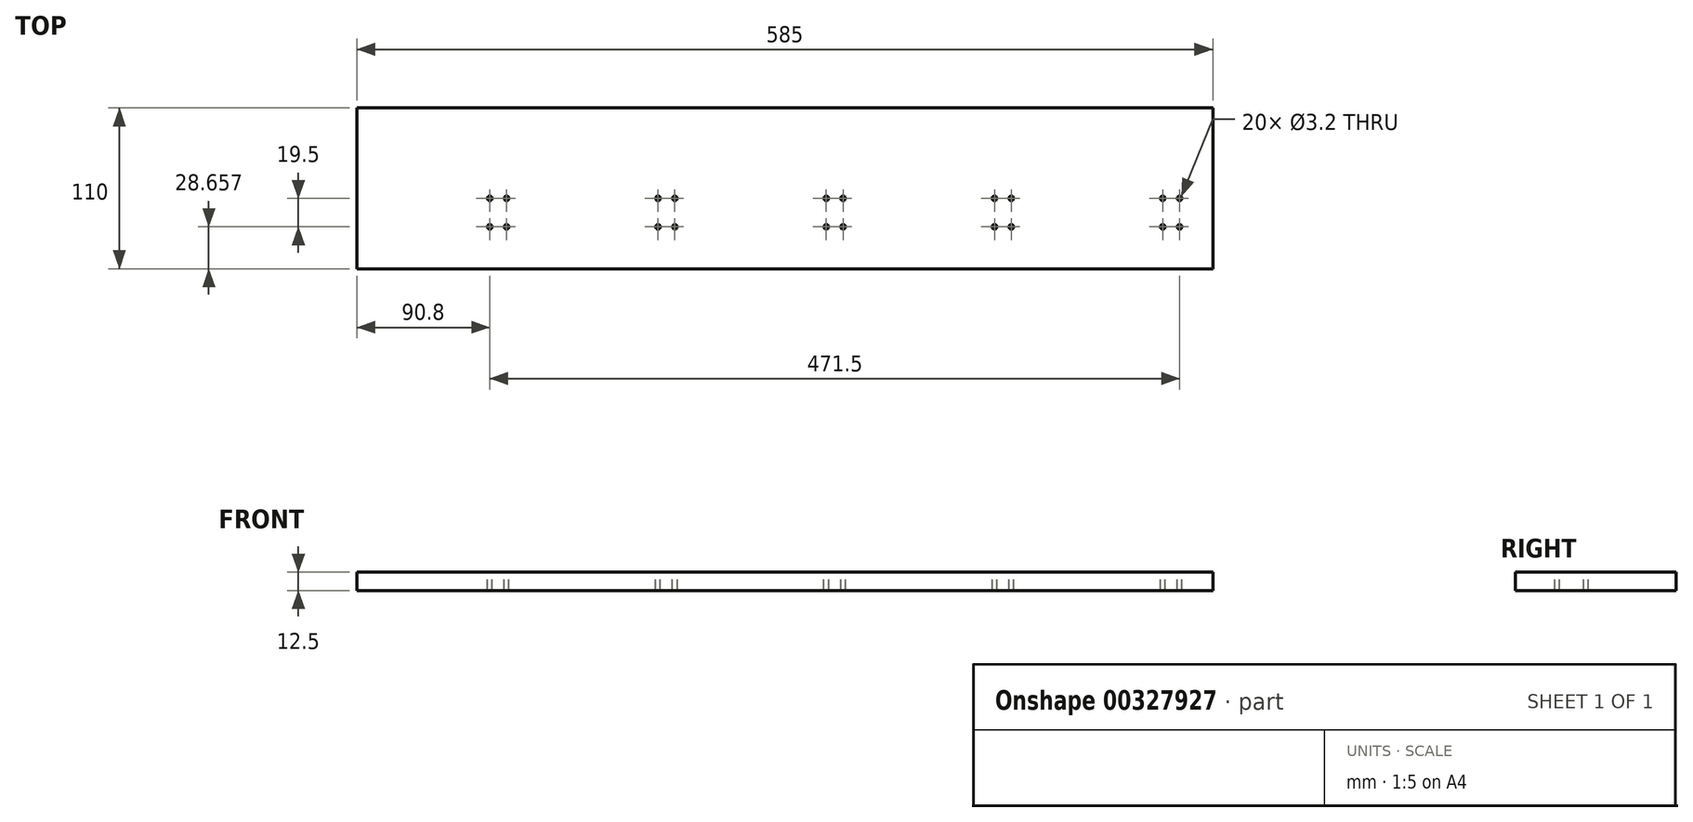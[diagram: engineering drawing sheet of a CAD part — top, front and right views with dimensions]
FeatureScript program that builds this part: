
annotation { "Feature Type Name" : "Feature", "Feature Type Description" : "" }
export const myFeature = defineFeature(function(context is Context, id is Id, definition is map)
    precondition{}
    {
        {
            var Q0;
            Q0=qCreatedBy(makeId("Top.planeOp"),FACE);
            var sketch = newSketch(context, id + "F0", { "sketchPlane" : qUnion([Q0])});
            skLineSegment(sketch, "E0.bottom", {"start": v(0, 0) * mm, "end": v(585, 0) * mm});
            skLineSegment(sketch, "E0.top", {"start": v(0, -110) * mm, "end": v(585, -110) * mm});
            skLineSegment(sketch, "E0.left", {"start": v(0, 0) * mm, "end": v(0, -110) * mm});
            skLineSegment(sketch, "E0.right", {"start": v(585, 0) * mm, "end": v(585, -110) * mm});
            skSolve(sketch);
        }
        {
            var Q0;
            Q0 = qSketchRegion(id + "F0", true);
            extrude(context, id + "F1", {"entities" : qUnion([Q0]), "depth" : 12.5 * mm});
        }
        {
            var Q0;
            Q0=makeQuery(id+"F1.opExtrude","CAP_FACE",FACE,{"disambiguationData":[OSD([sQuery(id+"F0.wireOp",EDGE,"E0.bottom"),sQuery(id+"F0.wireOp",EDGE,"E0.top"),sQuery(id+"F0.wireOp",EDGE,"E0.left"),sQuery(id+"F0.wireOp",EDGE,"E0.right")])],"isStart":false});
            var sketch = newSketch(context, id + "F2", { "sketchPlane" : qUnion([Q0])});
            skLineSegment(sketch, "E1.bottom", {"start": v(64.2, -65.1) * mm, "end": v(70.9, -65.1) * mm});
            skLineSegment(sketch, "E1.top", {"start": v(64.2, -78.1) * mm, "end": v(70.9, -78.1) * mm});
            skLineSegment(sketch, "E1.left", {"start": v(64.2, -65.1) * mm, "end": v(64.2, -78.1) * mm});
            skLineSegment(sketch, "E1.right", {"start": v(70.9, -65.1) * mm, "end": v(70.9, -78.1) * mm});
            skLineSegment(sketch, "E2.top", {"start": v(10, -95.2) * mm, "end": v(72.5, -95.2) * mm});
            skLineSegment(sketch, "E2.left", {"start": v(10, -10) * mm, "end": v(10, -95.2) * mm});
            skLineSegment(sketch, "E2.right", {"start": v(72.5, -10) * mm, "end": v(72.5, -95.2) * mm});
            skCircle(sketch, "E3", {"center": v(90.8, -61.84) * mm, "radius": 2 * mm});
            skCircle(sketch, "E4", {"center": v(90.8, -81.34) * mm, "radius": 2 * mm});
            skCircle(sketch, "E5", {"center": v(102.3, -61.84) * mm, "radius": 2 * mm});
            skCircle(sketch, "E6", {"center": v(102.3, -81.34) * mm, "radius": 2 * mm});
            skLineSegment(sketch, "E7", {"start": v(61.15, -71.6) * mm, "end": v(124.25, -71.6) * mm, "construction": true});
            skLineSegment(sketch, "E8.1.0.0", {"start": v(125, -95.2) * mm, "end": v(187.5, -95.2) * mm});
            skLineSegment(sketch, "E8.1.0.1", {"start": v(187.5, -10) * mm, "end": v(187.5, -95.2) * mm});
            skLineSegment(sketch, "E8.1.0.2", {"start": v(179.2, -65.1) * mm, "end": v(185.9, -65.1) * mm});
            skLineSegment(sketch, "E8.1.0.3", {"start": v(125, -10) * mm, "end": v(125, -95.2) * mm});
            skLineSegment(sketch, "E8.1.0.4", {"start": v(179.2, -78.1) * mm, "end": v(185.9, -78.1) * mm});
            skLineSegment(sketch, "E8.1.0.5", {"start": v(179.2, -65.1) * mm, "end": v(179.2, -78.1) * mm});
            skLineSegment(sketch, "E8.1.0.6", {"start": v(185.9, -65.1) * mm, "end": v(185.9, -78.1) * mm});
            skCircle(sketch, "E8.1.0.7", {"center": v(217.3, -81.34) * mm, "radius": 2 * mm});
            skLineSegment(sketch, "E8.1.0.8", {"start": v(176.15, -71.6) * mm, "end": v(239.25, -71.6) * mm, "construction": true});
            skCircle(sketch, "E8.1.0.9", {"center": v(217.3, -61.84) * mm, "radius": 2 * mm});
            skCircle(sketch, "E8.1.0.11", {"center": v(205.8, -81.34) * mm, "radius": 2 * mm});
            skCircle(sketch, "E8.1.0.12", {"center": v(205.8, -61.84) * mm, "radius": 2 * mm});
            skLineSegment(sketch, "E8.2.0.0", {"start": v(240, -95.2) * mm, "end": v(302.5, -95.2) * mm});
            skLineSegment(sketch, "E8.2.0.1", {"start": v(302.5, -10) * mm, "end": v(302.5, -95.2) * mm});
            skLineSegment(sketch, "E8.2.0.2", {"start": v(294.2, -65.1) * mm, "end": v(300.9, -65.1) * mm});
            skLineSegment(sketch, "E8.2.0.3", {"start": v(240, -10) * mm, "end": v(240, -95.2) * mm});
            skLineSegment(sketch, "E8.2.0.4", {"start": v(294.2, -78.1) * mm, "end": v(300.9, -78.1) * mm});
            skLineSegment(sketch, "E8.2.0.5", {"start": v(294.2, -65.1) * mm, "end": v(294.2, -78.1) * mm});
            skLineSegment(sketch, "E8.2.0.6", {"start": v(300.9, -65.1) * mm, "end": v(300.9, -78.1) * mm});
            skCircle(sketch, "E8.2.0.7", {"center": v(332.3, -81.34) * mm, "radius": 2 * mm});
            skLineSegment(sketch, "E8.2.0.8", {"start": v(291.15, -71.6) * mm, "end": v(354.25, -71.6) * mm, "construction": true});
            skCircle(sketch, "E8.2.0.9", {"center": v(332.3, -61.84) * mm, "radius": 2 * mm});
            skCircle(sketch, "E8.2.0.11", {"center": v(320.8, -81.34) * mm, "radius": 2 * mm});
            skCircle(sketch, "E8.2.0.12", {"center": v(320.8, -61.84) * mm, "radius": 2 * mm});
            skLineSegment(sketch, "E8.3.0.0", {"start": v(355, -95.2) * mm, "end": v(417.5, -95.2) * mm});
            skLineSegment(sketch, "E8.3.0.1", {"start": v(417.5, -10) * mm, "end": v(417.5, -95.2) * mm});
            skLineSegment(sketch, "E8.3.0.2", {"start": v(409.2, -65.1) * mm, "end": v(415.9, -65.1) * mm});
            skLineSegment(sketch, "E8.3.0.3", {"start": v(355, -10) * mm, "end": v(355, -95.2) * mm});
            skLineSegment(sketch, "E8.3.0.4", {"start": v(409.2, -78.1) * mm, "end": v(415.9, -78.1) * mm});
            skLineSegment(sketch, "E8.3.0.5", {"start": v(409.2, -65.1) * mm, "end": v(409.2, -78.1) * mm});
            skLineSegment(sketch, "E8.3.0.6", {"start": v(415.9, -65.1) * mm, "end": v(415.9, -78.1) * mm});
            skCircle(sketch, "E8.3.0.7", {"center": v(447.3, -81.34) * mm, "radius": 2 * mm});
            skLineSegment(sketch, "E8.3.0.8", {"start": v(406.15, -71.6) * mm, "end": v(469.25, -71.6) * mm, "construction": true});
            skCircle(sketch, "E8.3.0.9", {"center": v(447.3, -61.84) * mm, "radius": 2 * mm});
            skCircle(sketch, "E8.3.0.11", {"center": v(435.8, -81.34) * mm, "radius": 2 * mm});
            skCircle(sketch, "E8.3.0.12", {"center": v(435.8, -61.84) * mm, "radius": 2 * mm});
            skLineSegment(sketch, "E8.direction1", {"start": v(10, -95.2) * mm, "end": v(125, -95.2) * mm, "construction": true});
            skLineSegment(sketch, "E9.0.4.0", {"start": v(470, -95.2) * mm, "end": v(532.5, -95.2) * mm});
            skLineSegment(sketch, "E9.3.4.0", {"start": v(532.5, -10) * mm, "end": v(532.5, -95.2) * mm});
            skLineSegment(sketch, "E9.6.4.0", {"start": v(524.2, -65.1) * mm, "end": v(530.9, -65.1) * mm});
            skLineSegment(sketch, "E9.9.4.0", {"start": v(470, -10) * mm, "end": v(470, -95.2) * mm});
            skLineSegment(sketch, "E9.12.4.0", {"start": v(524.2, -78.1) * mm, "end": v(530.9, -78.1) * mm});
            skLineSegment(sketch, "E9.15.4.0", {"start": v(524.2, -65.1) * mm, "end": v(524.2, -78.1) * mm});
            skLineSegment(sketch, "E9.18.4.0", {"start": v(530.9, -65.1) * mm, "end": v(530.9, -78.1) * mm});
            skCircle(sketch, "E9.21.4.0", {"center": v(562.3, -81.34) * mm, "radius": 2 * mm});
            skLineSegment(sketch, "E9.23.4.0", {"start": v(521.15, -71.6) * mm, "end": v(584.25, -71.6) * mm, "construction": true});
            skCircle(sketch, "E9.26.4.0", {"center": v(562.3, -61.84) * mm, "radius": 2 * mm});
            skCircle(sketch, "E9.31.4.0", {"center": v(550.8, -81.34) * mm, "radius": 2 * mm});
            skCircle(sketch, "E9.33.4.0", {"center": v(550.8, -61.84) * mm, "radius": 2 * mm});
            skLineSegment(sketch, "E10", {"start": v(10, -10) * mm, "end": v(72.5, -10) * mm});
            skLineSegment(sketch, "E11", {"start": v(125, -10) * mm, "end": v(187.5, -10) * mm});
            skLineSegment(sketch, "E12", {"start": v(240, -10) * mm, "end": v(302.5, -10) * mm});
            skLineSegment(sketch, "E13", {"start": v(355, -10) * mm, "end": v(417.5, -10) * mm});
            skLineSegment(sketch, "E14", {"start": v(470, -10) * mm, "end": v(532.5, -10) * mm});
            skSolve(sketch);
        }
        {
            var Q0;
            Q0=sQuery(id+"F2.wireOp",VERTEX,"E4.center");
            var Q1;
            Q1=sQuery(id+"F2.wireOp",VERTEX,"E3.center");
            var Q2;
            Q2=sQuery(id+"F2.wireOp",VERTEX,"E5.center");
            var Q3;
            Q3=sQuery(id+"F2.wireOp",VERTEX,"E6.center");
            var Q4;
            Q4=sQuery(id+"F2.wireOp",VERTEX,"E8.1.0.12.center");
            var Q5;
            Q5=sQuery(id+"F2.wireOp",VERTEX,"E8.1.0.9.center");
            var Q6;
            Q6=sQuery(id+"F2.wireOp",VERTEX,"E8.1.0.11.center");
            var Q7;
            Q7=sQuery(id+"F2.wireOp",VERTEX,"E8.1.0.7.center");
            var Q8;
            Q8=sQuery(id+"F2.wireOp",VERTEX,"E8.2.0.12.center");
            var Q9;
            Q9=sQuery(id+"F2.wireOp",VERTEX,"E8.2.0.11.center");
            var Q10;
            Q10=sQuery(id+"F2.wireOp",VERTEX,"E8.2.0.9.center");
            var Q11;
            Q11=sQuery(id+"F2.wireOp",VERTEX,"E8.2.0.7.center");
            var Q12;
            Q12=sQuery(id+"F2.wireOp",VERTEX,"E8.3.0.12.center");
            var Q13;
            Q13=sQuery(id+"F2.wireOp",VERTEX,"E8.3.0.9.center");
            var Q14;
            Q14=sQuery(id+"F2.wireOp",VERTEX,"E8.3.0.11.center");
            var Q15;
            Q15=sQuery(id+"F2.wireOp",VERTEX,"E8.3.0.7.center");
            var Q16;
            Q16=sQuery(id+"F2.wireOp",VERTEX,"E9.33.4.0.center");
            var Q17;
            Q17=sQuery(id+"F2.wireOp",VERTEX,"E9.26.4.0.center");
            var Q18;
            Q18=sQuery(id+"F2.wireOp",VERTEX,"E9.21.4.0.center");
            var Q19;
            Q19=sQuery(id+"F2.wireOp",VERTEX,"E9.31.4.0.center");
            var Q20;
            Q20=makeQuery(id+"F1.opExtrude","SWEPT_BODY",BODY,{"disambiguationData":[OSD([sQuery(id+"F0.wireOp",EDGE,"E0.bottom"),sQuery(id+"F0.wireOp",EDGE,"E0.top"),sQuery(id+"F0.wireOp",EDGE,"E0.left"),sQuery(id+"F0.wireOp",EDGE,"E0.right")])]});
            hole(context, id + "F3", {"style" : HoleStyle.SIMPLE, "endStyle" : HoleEndStyle.THROUGH, "standardTappedOrClearance" : lookupTablePath({ "standard" : "ISO", "engagement" : "75%", "pitch" : "0.75 mm", "size" : "M4", "type" : "Tapped" }), "standardBlindInLast" : lookupTablePath({ "standard" : "ISO", "engagement" : "75%", "pitch" : "0.75 mm", "size" : "M4", "type" : "Tapped" }), "holeDiameter" : 3.2 * mm, "showTappedDepth" : true, "tappedDepth" : 8 * mm, "tapClearance" : 3, "locations" : qUnion([Q0, Q1, Q2, Q3, Q4, Q5, Q6, Q7, Q8, Q9, Q10, Q11, Q12, Q13, Q14, Q15, Q16, Q17, Q18, Q19]), "scope" : qUnion([Q20])});
        }
    });
